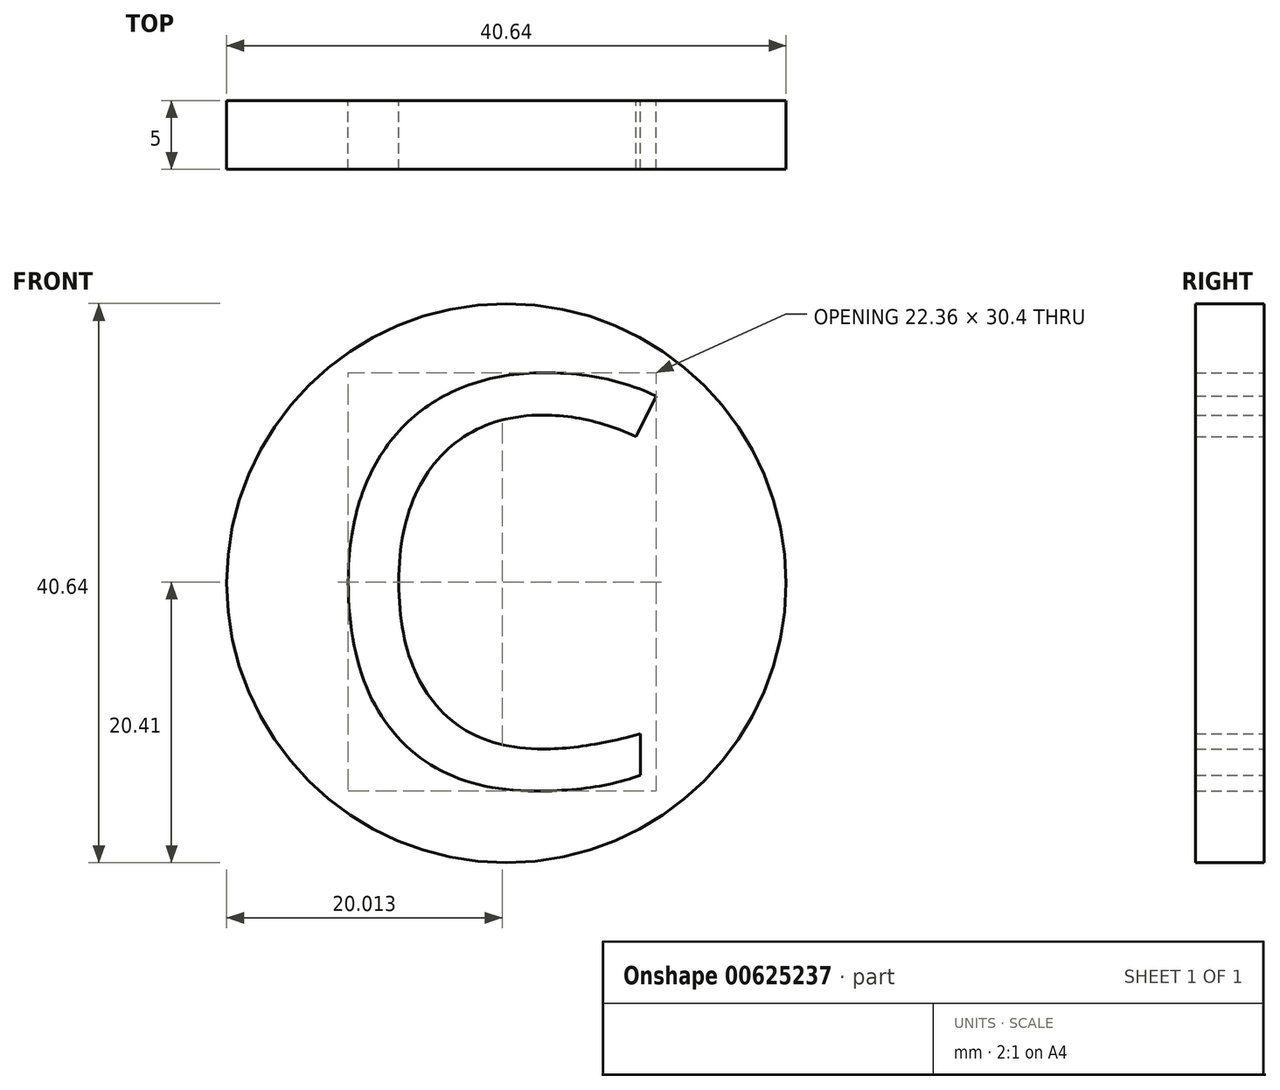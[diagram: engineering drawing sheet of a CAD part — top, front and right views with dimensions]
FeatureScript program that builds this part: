
annotation { "Feature Type Name" : "Feature", "Feature Type Description" : "" }
export const myFeature = defineFeature(function(context is Context, id is Id, definition is map)
    precondition{}
    {
        {
            var Q0;
            Q0=qCreatedBy(makeId("Front.planeOp"),FACE);
            var sketch = newSketch(context, id + "F0", { "sketchPlane" : qUnion([Q0])});
            skCircle(sketch, "E0", {"center": v(0, 0) * mm, "radius": 20.32 * mm});
            skText(sketch, "E1", { "text": "C\n", "fontName": "OpenSans-Regular.ttf"});
            const initialGuessF0  = {"E1": [-0.01402, -0.0147, 1, 0, 0.02982]};
            skSetInitialGuess(sketch, initialGuessF0);
            skSolve(sketch);
        }
        {
            var Q0;
            Q0=makeQuery(id+"F0.imprint","IMPRINT",FACE,{"disambiguationData":[TD([[makeQuery(id+"F0.imprint","IMPRINT",EDGE,{"derivedFrom":sQuery(id+"F0.wireOp",EDGE,"E0")}),1.0]])]});
            extrude(context, id + "F1", {"entities" : qUnion([Q0]), "depth" : 5 * mm, "offsetDistance" : 25 * mm});
        }
    });
